# Revit family: Deca_Acessório de louça_Jader Almeida_A.302
name_source: partatom
category: Plumbing Fixtures
units: mm (PartAtom-declared; Revit-internal decimal feet)

## family parameters
Cut with Voids When Loaded = No
Host = Face
Part Type = Normal
Room Calculation Point = No
Round Connector Dimension = Use Diameter
Shared = No

## types (2) — shared parameters
Acompanha o Produto = -
Aprovado por = quattroD
Atendimento ao Cliente = 0800-0117073
Categoria = ACESSORIOS
Composição Anel Vedação = -
Composição Assento = -
Composição Básica = Argila, feldspato, caulim, vidrados e corantes inorgânicos.
Composição Componente = Aço inoxidável, elastômeros e plásticos de engenharia.
Consumo = -
Cor Interna = -
Cor Secundária = -
Cores Componente = Não Possui
Criado por = quattroD
Código Pai = A.302
Default Elevation = 1.1 m
Description = ACESSÓRIO DE LOUÇA
Informações Complementares = -
Itens de Instalação = -
Linha = Jader Almeida
Manufacturer = Deca
Norma = Não Possui
Peso Líquido (Kg) = 2.093
Pressão máx. funcionamento = -
Pressão mín. Aquec. Acúmulo = -
Pressão mín. Aquec. Passagem = -
Pressão mín. funcionamento = -
Saída de Esgoto = -
Segmento = Banheiro Luxo
Tipo de dispositivo economizador = -
Tipo de mecanismo utilizado = -
Tipo de rosca de entrada = -
Tipo de rosca de saída = -
URL = www.deca.com.br
Vazão na Pressão máx. (L/min) = -
Vazão na Pressão mín. (L/min) = -

## per-type parameters (varying)
| type | Cor Principal | Material | Model |
| A.302.17_Branco | Branco | Deca_Branco | A.302.17 |
| A.302.94_Ébano Fosco | Ébano fosco | Deca_Ébano Fosco | A.302.94 |

## geometry (parser evidence)
native form markers: Sweep x2
no freeform markers — native parametric forms only
